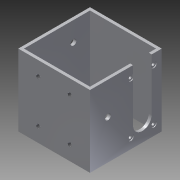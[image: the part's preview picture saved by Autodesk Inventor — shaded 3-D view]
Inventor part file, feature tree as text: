
AUTODESK INVENTOR PART (.ipt)
format: ipt  version: 2013 (Build 170138000, 138)  size: 169,984 bytes
history: native  units: mm
features: thread x4, sketch x4, hole x3, other x1, extrude x1
ambient origin geometry x1: Origin
feature tree (13):
  other  "ソリッド1"
  extrude  "押し出し1"  Depth=50.0mm
  hole  "穴1"  [1 undecoded]
  hole  "穴6"  [1 undecoded]
  hole  "穴13"  [1 undecoded]
  thread  "ねじ13"
  thread  "ねじ14"
  thread  "ねじ15"
  thread  "ねじ16"
  sketch  "スケッチ1"
  sketch  "スケッチ3"
  sketch  "スケッチ11"
  sketch  "スケッチ18"
note: 3 required parameter values undecoded (feature->parameter linkage not recoverable at this tier; creation-order binding heuristic only, values carry confidence <= 0.55)
